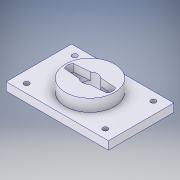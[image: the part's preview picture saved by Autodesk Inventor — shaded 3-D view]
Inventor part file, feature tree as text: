
AUTODESK INVENTOR PART (.ipt)
format: ipt  version: 2017 (Build 210142000, 142)  size: 161,280 bytes
history: native  units: in
note: dims shown in document units (in); Inventor stores cm internally (conversion verified against a paired STEP export)
features: extrude x3, sketch x3
ambient origin geometry x8: Origin, YZ Plane, XZ Plane, XY Plane, X Axis, Y Axis, Z Axis, Center Point
bodies: Solid1 (feature_tree)
feature tree (6):
  extrude  "Extrusion1"  Depth=1.2598in
  extrude  "Extrusion2"  Depth=0.1672in
  extrude  "Extrusion3"  Depth=0.1447in
  sketch  "Sketch1"  dims[d0=1.9685in d1=1.2598in]
  sketch  "Sketch2"  dims[d2=0.2263in d3=0.1672in]
  sketch  "Sketch3"  dims[d4=0.0984in d5=0.2953in d6=0.1575in d7=0.0in d8=0.9449in d9=0.2756in d10=0.2756in d11=0.0591in d12=0.0591in d13=0.0915in d14=0.0in d15=0.0221in d16=0.2756in d17=0.1133in d18=0.1312in d20=0.0896in d21=0.0323in d22=0.1447in d23=0.0in]
